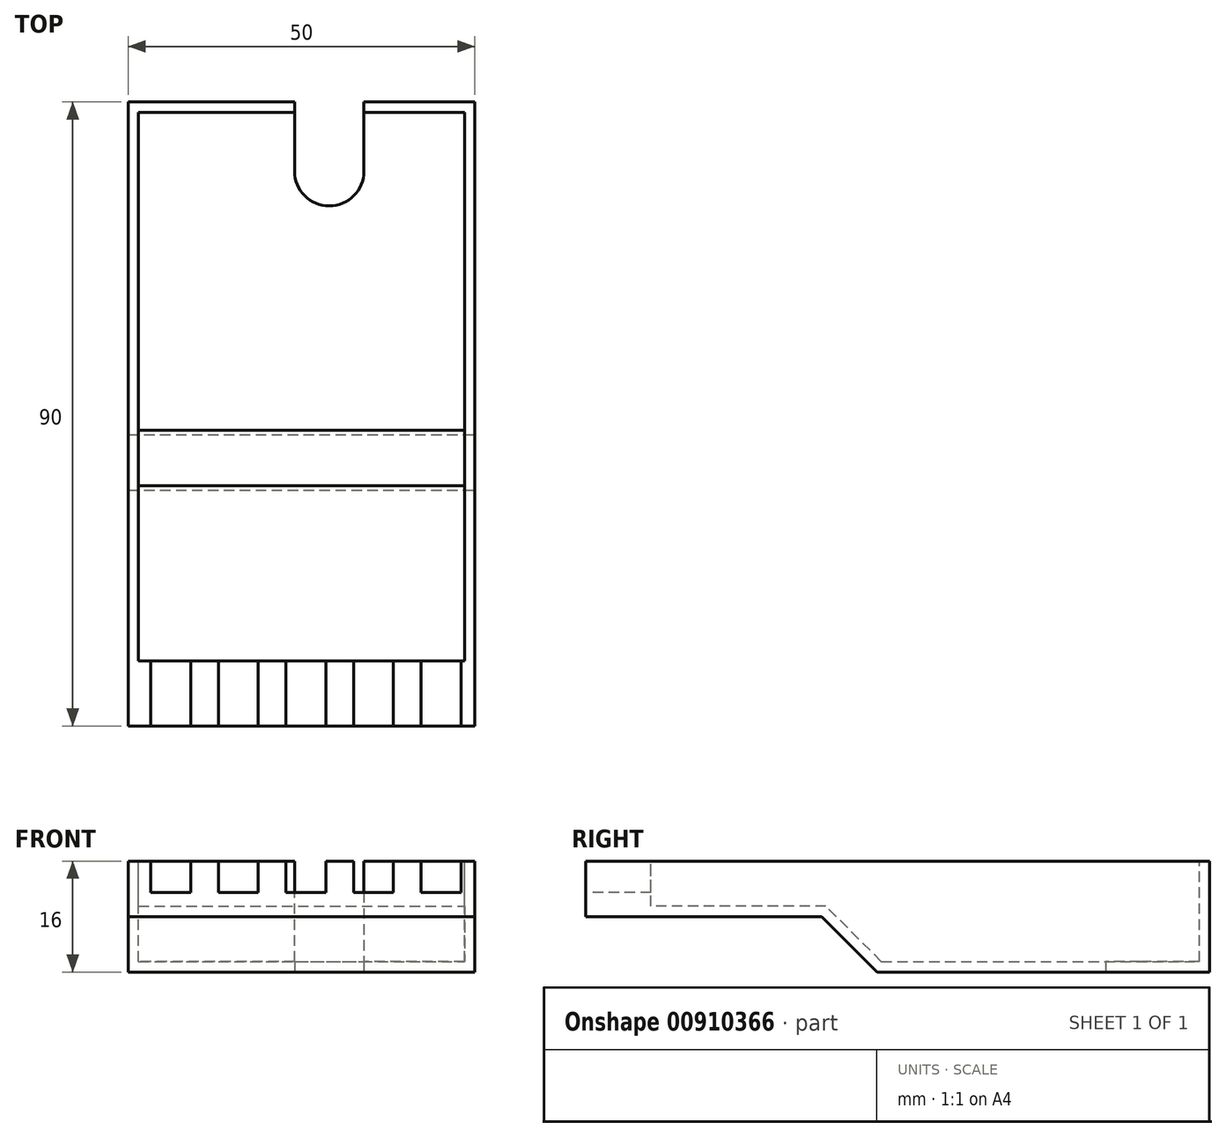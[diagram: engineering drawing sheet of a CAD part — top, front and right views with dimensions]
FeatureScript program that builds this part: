
annotation { "Feature Type Name" : "Feature", "Feature Type Description" : "" }
export const myFeature = defineFeature(function(context is Context, id is Id, definition is map)
    precondition{}
    {
        {
            var Q0;
            Q0=qCreatedBy(makeId("Top.planeOp"),FACE);
            var sketch = newSketch(context, id + "F0", { "sketchPlane" : qUnion([Q0])});
            skLineSegment(sketch, "E0.bottom", {"start": v(0, 0) * mm, "end": v(50, 0) * mm});
            skLineSegment(sketch, "E0.top", {"start": v(0, 90) * mm, "end": v(24, 90) * mm});
            skLineSegment(sketch, "E0.left", {"start": v(0, 0) * mm, "end": v(0, 90) * mm});
            skLineSegment(sketch, "E0.right", {"start": v(50, 0) * mm, "end": v(50, 90) * mm});
            skLineSegment(sketch, "E1", {"start": v(34, 90) * mm, "end": v(34, 80) * mm});
            skLineSegment(sketch, "E2", {"start": v(24, 80) * mm, "end": v(24, 90) * mm});
            skLineSegment(sketch, "E3.trimOffspring", {"start": v(34, 90) * mm, "end": v(50, 90) * mm});
            skArc(sketch, "E4", {"start": v(24, 80) * mm, "mid": v(29, 75) * mm, "end": v(34, 80) * mm});
            skSolve(sketch);
        }
        {
            var Q0;
            Q0 = qSketchRegion(id + "F0", true);
            extrude(context, id + "F1", {"entities" : qUnion([Q0]), "depth" : 16 * mm, "offsetDistance" : 25.4 * mm});
        }
        {
            var Q0;
            Q0=makeQuery(id+"F1.opExtrude","CAP_FACE",FACE,{"disambiguationData":[OSD([sQuery(id+"F0.wireOp",EDGE,"E0.bottom"),sQuery(id+"F0.wireOp",EDGE,"E0.top"),sQuery(id+"F0.wireOp",EDGE,"E0.left"),sQuery(id+"F0.wireOp",EDGE,"E0.right")])],"isStart":false});
            var sketch = newSketch(context, id + "F2", { "sketchPlane" : qUnion([Q0])});
            skLineSegment(sketch, "E5.bottom", {"start": v(1.5, 88.5) * mm, "end": v(48.5, 88.5) * mm});
            skLineSegment(sketch, "E5.top", {"start": v(1.5, 9.4) * mm, "end": v(48.5, 9.4) * mm});
            skLineSegment(sketch, "E5.left", {"start": v(1.5, 88.5) * mm, "end": v(1.5, 9.4) * mm});
            skLineSegment(sketch, "E5.right", {"start": v(48.5, 88.5) * mm, "end": v(48.5, 9.4) * mm});
            skSolve(sketch);
        }
        {
            var Q0;
            Q0 = qSketchRegion(id + "F2", true);
            var Q1;
            Q1=makeQuery(id+"F1.opExtrude","CAP_FACE",FACE,{"disambiguationData":[OSD([sQuery(id+"F0.wireOp",EDGE,"E0.bottom"),sQuery(id+"F0.wireOp",EDGE,"E0.top"),sQuery(id+"F0.wireOp",EDGE,"E0.left"),sQuery(id+"F0.wireOp",EDGE,"E0.right")])],"isStart":true});
            extrude(context, id + "F3", {"entities" : qUnion([Q0]), "operationType" : NewBodyOperationType.REMOVE, "endBound" : BoundingType.UP_TO_SURFACE, "oppositeDirection" : true, "depth" : 25.4 * mm, "endBoundEntityFace" : qUnion([Q1]), "hasOffset" : true, "offsetDistance" : 1.5 * mm});
        }
        {
            var Q0;
            Q0=makeQuery(id+"F1.opExtrude","CAP_FACE",FACE,{"disambiguationData":[OSD([sQuery(id+"F0.wireOp",EDGE,"E0.bottom"),sQuery(id+"F0.wireOp",EDGE,"E0.top"),sQuery(id+"F0.wireOp",EDGE,"E0.left"),sQuery(id+"F0.wireOp",EDGE,"E0.right")])],"isStart":false});
            var sketch = newSketch(context, id + "F4", { "sketchPlane" : qUnion([Q0])});
            skLineSegment(sketch, "E6.bottom", {"start": v(48, 9.4) * mm, "end": v(42.25, 9.4) * mm});
            skLineSegment(sketch, "E6.top", {"start": v(48, 0) * mm, "end": v(42.25, 0) * mm});
            skLineSegment(sketch, "E6.left", {"start": v(48, 9.4) * mm, "end": v(48, 0) * mm});
            skLineSegment(sketch, "E6.right", {"start": v(42.25, 9.4) * mm, "end": v(42.25, 0) * mm});
            skLineSegment(sketch, "E7.1.0.0", {"start": v(38.25, 9.4) * mm, "end": v(38.25, 0) * mm});
            skLineSegment(sketch, "E7.1.0.1", {"start": v(38.25, 0) * mm, "end": v(32.5, 0) * mm});
            skLineSegment(sketch, "E7.1.0.2", {"start": v(32.5, 9.4) * mm, "end": v(32.5, 0) * mm});
            skLineSegment(sketch, "E7.1.0.3", {"start": v(38.25, 9.4) * mm, "end": v(32.5, 9.4) * mm});
            skLineSegment(sketch, "E7.2.0.0", {"start": v(28.5, 9.4) * mm, "end": v(28.5, 0) * mm});
            skLineSegment(sketch, "E7.2.0.1", {"start": v(28.5, 0) * mm, "end": v(22.75, 0) * mm});
            skLineSegment(sketch, "E7.2.0.2", {"start": v(22.75, 9.4) * mm, "end": v(22.75, 0) * mm});
            skLineSegment(sketch, "E7.2.0.3", {"start": v(28.5, 9.4) * mm, "end": v(22.75, 9.4) * mm});
            skLineSegment(sketch, "E7.3.0.0", {"start": v(18.75, 9.4) * mm, "end": v(18.75, 0) * mm});
            skLineSegment(sketch, "E7.3.0.1", {"start": v(18.75, 0) * mm, "end": v(13, 0) * mm});
            skLineSegment(sketch, "E7.3.0.2", {"start": v(13, 9.4) * mm, "end": v(13, 0) * mm});
            skLineSegment(sketch, "E7.3.0.3", {"start": v(18.75, 9.4) * mm, "end": v(13, 9.4) * mm});
            skLineSegment(sketch, "E7.4.0.0", {"start": v(9, 9.4) * mm, "end": v(9, 0) * mm});
            skLineSegment(sketch, "E7.4.0.1", {"start": v(9, 0) * mm, "end": v(3.25, 0) * mm});
            skLineSegment(sketch, "E7.4.0.2", {"start": v(3.25, 9.4) * mm, "end": v(3.25, 0) * mm});
            skLineSegment(sketch, "E7.4.0.3", {"start": v(9, 9.4) * mm, "end": v(3.25, 9.4) * mm});
            skLineSegment(sketch, "E7.direction1", {"start": v(42.25, 0) * mm, "end": v(32.5, 0) * mm, "construction": true});
            skLineSegment(sketch, "E8", {"start": v(45.12, 0) * mm, "end": v(45.12, 9.4) * mm, "construction": true});
            skSolve(sketch);
        }
        {
            var Q0;
            Q0 = qSketchRegion(id + "F4", true);
            extrude(context, id + "F5", {"entities" : qUnion([Q0]), "operationType" : NewBodyOperationType.REMOVE, "oppositeDirection" : true, "depth" : 4.5 * mm, "offsetDistance" : 25.4 * mm});
        }
        {
            var Q0;
            Q0=makeQuery(id+"F1.opExtrude","SWEPT_FACE",FACE,{"disambiguationData":[OSD([sQuery(id+"F0.wireOp",EDGE,"E0.right")])]});
            var sketch = newSketch(context, id + "F6", { "sketchPlane" : qUnion([Q0])});
            skLineSegment(sketch, "E9", {"start": v(0, 0) * mm, "end": v(0, 8) * mm});
            skLineSegment(sketch, "E10", {"start": v(0, 8) * mm, "end": v(34, 8) * mm});
            skLineSegment(sketch, "E11", {"start": v(34, 8) * mm, "end": v(42, 0) * mm});
            skLineSegment(sketch, "E12", {"start": v(42, 0) * mm, "end": v(0, 0) * mm});
            skSolve(sketch);
        }
        {
            var Q0;
            Q0 = qSketchRegion(id + "F6", true);
            extrude(context, id + "F7", {"entities" : qUnion([Q0]), "operationType" : NewBodyOperationType.REMOVE, "endBound" : BoundingType.THROUGH_ALL, "oppositeDirection" : true, "depth" : 25.4 * mm, "offsetDistance" : 25.4 * mm});
        }
        {
            var Q0;
            Q0=makeQuery(id+"F1.opExtrude","SWEPT_FACE",FACE,{"disambiguationData":[OSD([sQuery(id+"F0.wireOp",EDGE,"E0.left")])]});
            var sketch = newSketch(context, id + "F8", { "sketchPlane" : qUnion([Q0])});
            skLineSegment(sketch, "E13.0", {"start": v(-34, 8) * mm, "end": v(0, 8) * mm});
            skLineSegment(sketch, "E13.1", {"start": v(-42, 0) * mm, "end": v(-34, 8) * mm});
            skLineSegment(sketch, "E14", {"start": v(-42, 0) * mm, "end": v(-44.12, 0) * mm});
            skLineSegment(sketch, "E15", {"start": v(-44.12, 0) * mm, "end": v(-34.62, 9.5) * mm});
            skLineSegment(sketch, "E16", {"start": v(-34.62, 9.5) * mm, "end": v(0, 9.5) * mm});
            skLineSegment(sketch, "E17", {"start": v(0, 9.5) * mm, "end": v(0, 8) * mm});
            skLineSegment(sketch, "E18", {"start": v(-42, 0) * mm, "end": v(-43.06, 1.06) * mm, "construction": true});
            skSolve(sketch);
        }
        {
            var Q0;
            Q0 = qSketchRegion(id + "F8", true);
            var Q1;
            Q1=makeQuery(id+"F3.boolean.opBoolean","COPY",FACE,{"derivedFrom":makeQuery(id+"F3.opExtrude","SWEPT_FACE",FACE,{"disambiguationData":[OSD([sQuery(id+"F2.wireOp",EDGE,"E5.right")])]})});
            extrude(context, id + "F9", {"entities" : qUnion([Q0]), "operationType" : NewBodyOperationType.ADD, "endBound" : BoundingType.UP_TO_SURFACE, "oppositeDirection" : true, "depth" : 25.4 * mm, "endBoundEntityFace" : qUnion([Q1]), "offsetDistance" : 25.4 * mm});
        }
    });
